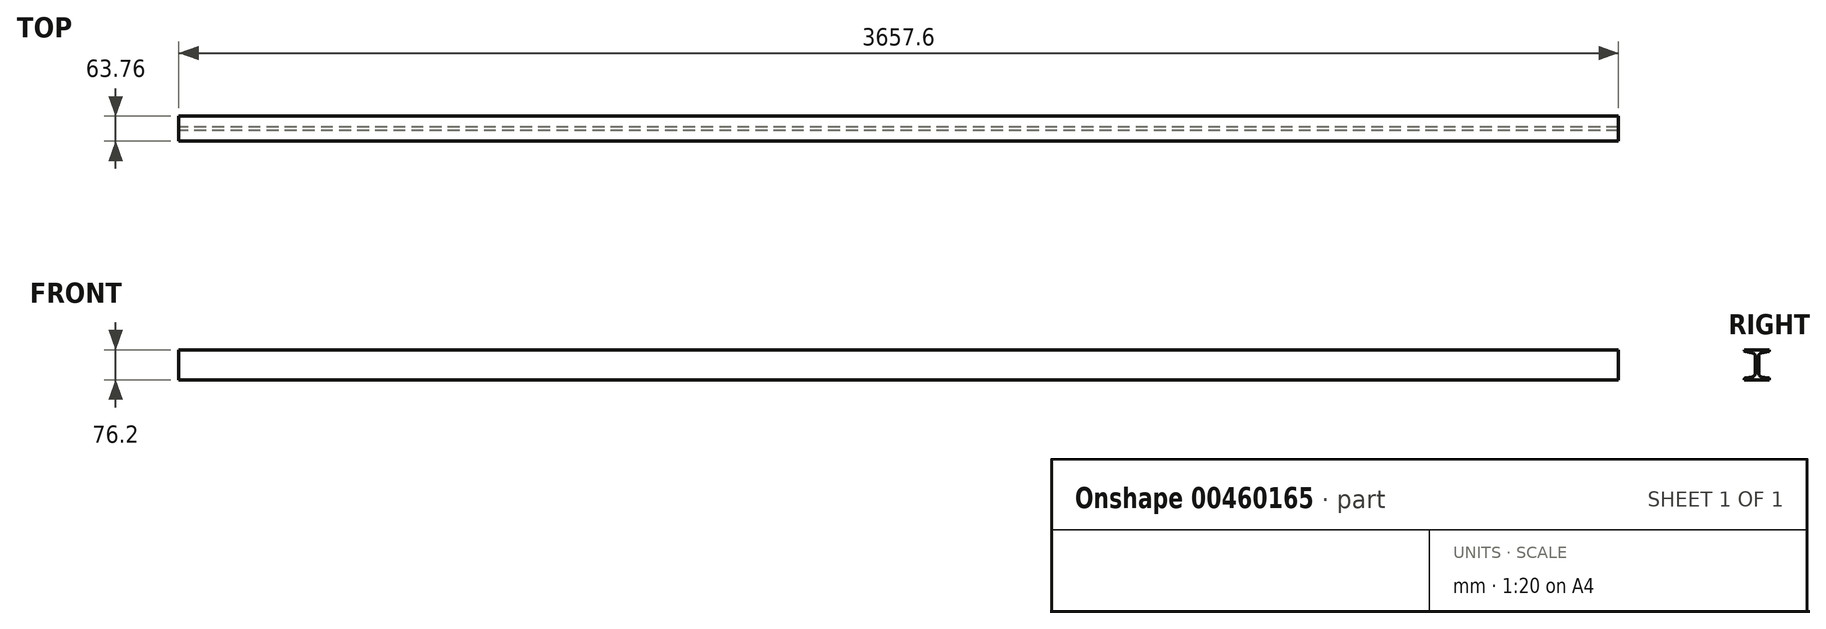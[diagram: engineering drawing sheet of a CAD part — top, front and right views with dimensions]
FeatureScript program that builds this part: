
annotation { "Feature Type Name" : "Feature", "Feature Type Description" : "" }
export const myFeature = defineFeature(function(context is Context, id is Id, definition is map)
    precondition{}
    {
        {
            var Q0;
            Q0=qCreatedBy(makeId("Right.planeOp"),FACE);
            var sketch = newSketch(context, id + "F0", { "sketchPlane" : qUnion([Q0])});
            skArc(sketch, "E0", {"start": v(31.88, 36) * mm, "mid": v(31.3, 34.4) * mm, "end": v(29.82, 33.55) * mm});
            skLineSegment(sketch, "E1", {"start": v(29.82, 33.55) * mm, "end": v(11.18, 30.27) * mm});
            skArc(sketch, "E2", {"start": v(11.18, 30.27) * mm, "mid": v(6.34, 27.47) * mm, "end": v(4.43, 22.23) * mm});
            skLineSegment(sketch, "E3", {"start": v(4.43, 22.23) * mm, "end": v(4.43, -22.23) * mm});
            skArc(sketch, "E4", {"start": v(4.43, -22.23) * mm, "mid": v(6.34, -27.47) * mm, "end": v(11.18, -30.27) * mm});
            skLineSegment(sketch, "E5", {"start": v(11.18, -30.27) * mm, "end": v(29.82, -33.55) * mm});
            skArc(sketch, "E6", {"start": v(29.82, -33.55) * mm, "mid": v(31.3, -34.4) * mm, "end": v(31.88, -36) * mm});
            skLineSegment(sketch, "E7", {"start": v(31.88, -36) * mm, "end": v(31.88, -38.1) * mm});
            skLineSegment(sketch, "E8", {"start": v(31.88, -38.1) * mm, "end": v(-31.88, -38.1) * mm});
            skLineSegment(sketch, "E9", {"start": v(-31.88, -38.1) * mm, "end": v(-31.88, -36) * mm});
            skArc(sketch, "E10", {"start": v(-31.88, -36) * mm, "mid": v(-31.3, -34.4) * mm, "end": v(-29.82, -33.55) * mm});
            skLineSegment(sketch, "E11", {"start": v(-29.82, -33.55) * mm, "end": v(-11.18, -30.27) * mm});
            skArc(sketch, "E12", {"start": v(-11.18, -30.27) * mm, "mid": v(-6.34, -27.47) * mm, "end": v(-4.43, -22.23) * mm});
            skLineSegment(sketch, "E13", {"start": v(-4.43, -22.23) * mm, "end": v(-4.43, 22.23) * mm});
            skArc(sketch, "E14", {"start": v(-4.43, 22.23) * mm, "mid": v(-6.34, 27.47) * mm, "end": v(-11.18, 30.27) * mm});
            skLineSegment(sketch, "E15", {"start": v(-11.18, 30.27) * mm, "end": v(-29.82, 33.55) * mm});
            skArc(sketch, "E16", {"start": v(-29.82, 33.55) * mm, "mid": v(-31.3, 34.4) * mm, "end": v(-31.88, 36) * mm});
            skLineSegment(sketch, "E17", {"start": v(-31.88, 36) * mm, "end": v(-31.88, 38.1) * mm});
            skLineSegment(sketch, "E18", {"start": v(-31.88, 38.1) * mm, "end": v(31.88, 38.1) * mm});
            skLineSegment(sketch, "E19", {"start": v(31.88, 38.1) * mm, "end": v(31.88, 36) * mm});
            skSolve(sketch);
        }
        {
            var Q0;
            Q0 = qSketchRegion(id + "F0", true);
            extrude(context, id + "F1", {"entities" : qUnion([Q0]), "endBound" : BoundingType.SYMMETRIC, "depth" : 3657.6 * mm});
        }
    });
